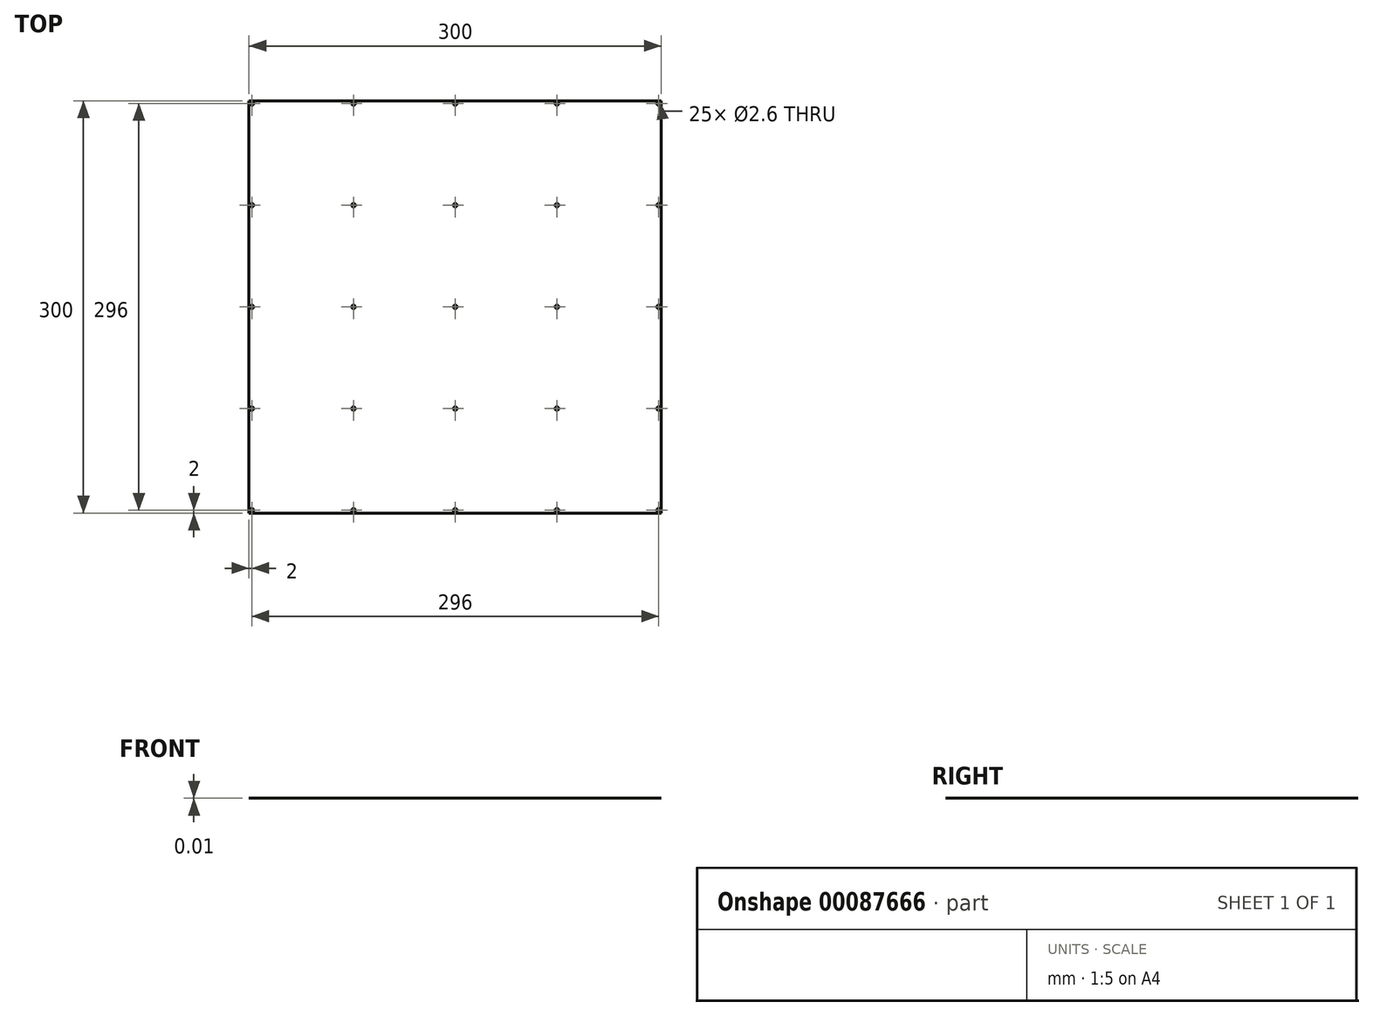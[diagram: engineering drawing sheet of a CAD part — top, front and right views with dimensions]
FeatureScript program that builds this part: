
annotation { "Feature Type Name" : "Feature", "Feature Type Description" : "" }
export const myFeature = defineFeature(function(context is Context, id is Id, definition is map)
    precondition{}
    {
        {
            var Q0;
            Q0=qCreatedBy(makeId("Top.planeOp"),FACE);
            var sketch = newSketch(context, id + "F0", { "sketchPlane" : qUnion([Q0])});
            skLineSegment(sketch, "E0.bottom", {"start": v(-150, 150) * mm, "end": v(150, 150) * mm});
            skLineSegment(sketch, "E0.top", {"start": v(-150, -150) * mm, "end": v(150, -150) * mm});
            skLineSegment(sketch, "E0.left", {"start": v(-150, 150) * mm, "end": v(-150, -150) * mm});
            skLineSegment(sketch, "E0.right", {"start": v(150, 150) * mm, "end": v(150, -150) * mm});
            skPoint(sketch, "E0.middle", {"position": v(0, 0) * mm});
            skCircle(sketch, "E1", {"center": v(-148, -148) * mm, "radius": 1.3 * mm});
            skCircle(sketch, "E2.0.1.0", {"center": v(-148, -74) * mm, "radius": 1.3 * mm});
            skCircle(sketch, "E2.0.2.0", {"center": v(-148, 0) * mm, "radius": 1.3 * mm});
            skCircle(sketch, "E2.0.3.0", {"center": v(-148, 74) * mm, "radius": 1.3 * mm});
            skCircle(sketch, "E2.0.4.0", {"center": v(-148, 148) * mm, "radius": 1.3 * mm});
            skCircle(sketch, "E2.1.0.0", {"center": v(-74, -148) * mm, "radius": 1.3 * mm});
            skCircle(sketch, "E2.1.1.0", {"center": v(-74, -74) * mm, "radius": 1.3 * mm});
            skCircle(sketch, "E2.1.2.0", {"center": v(-74, 0) * mm, "radius": 1.3 * mm});
            skCircle(sketch, "E2.1.3.0", {"center": v(-74, 74) * mm, "radius": 1.3 * mm});
            skCircle(sketch, "E2.1.4.0", {"center": v(-74, 148) * mm, "radius": 1.3 * mm});
            skCircle(sketch, "E2.2.0.0", {"center": v(0, -148) * mm, "radius": 1.3 * mm});
            skCircle(sketch, "E2.2.1.0", {"center": v(0, -74) * mm, "radius": 1.3 * mm});
            skCircle(sketch, "E2.2.2.0", {"center": v(0, 0) * mm, "radius": 1.3 * mm});
            skCircle(sketch, "E2.2.3.0", {"center": v(0, 74) * mm, "radius": 1.3 * mm});
            skCircle(sketch, "E2.2.4.0", {"center": v(0, 148) * mm, "radius": 1.3 * mm});
            skCircle(sketch, "E2.3.0.0", {"center": v(74, -148) * mm, "radius": 1.3 * mm});
            skCircle(sketch, "E2.3.1.0", {"center": v(74, -74) * mm, "radius": 1.3 * mm});
            skCircle(sketch, "E2.3.2.0", {"center": v(74, 0) * mm, "radius": 1.3 * mm});
            skCircle(sketch, "E2.3.3.0", {"center": v(74, 74) * mm, "radius": 1.3 * mm});
            skCircle(sketch, "E2.3.4.0", {"center": v(74, 148) * mm, "radius": 1.3 * mm});
            skCircle(sketch, "E2.4.0.0", {"center": v(148, -148) * mm, "radius": 1.3 * mm});
            skCircle(sketch, "E2.4.1.0", {"center": v(148, -74) * mm, "radius": 1.3 * mm});
            skCircle(sketch, "E2.4.2.0", {"center": v(148, 0) * mm, "radius": 1.3 * mm});
            skCircle(sketch, "E2.4.3.0", {"center": v(148, 74) * mm, "radius": 1.3 * mm});
            skCircle(sketch, "E2.4.4.0", {"center": v(148, 148) * mm, "radius": 1.3 * mm});
            skLineSegment(sketch, "E2.direction1", {"start": v(-148, -148) * mm, "end": v(-74, -148) * mm, "construction": true});
            skLineSegment(sketch, "E2.direction2", {"start": v(-148, -148) * mm, "end": v(-148, -74) * mm, "construction": true});
            skSolve(sketch);
        }
        {
            var Q0;
            Q0 = qSketchRegion(id + "F0", true);
            extrude(context, id + "F1", {"entities" : qUnion([Q0]), "depth" : 1 / 101.6 * mm});
        }
    });
